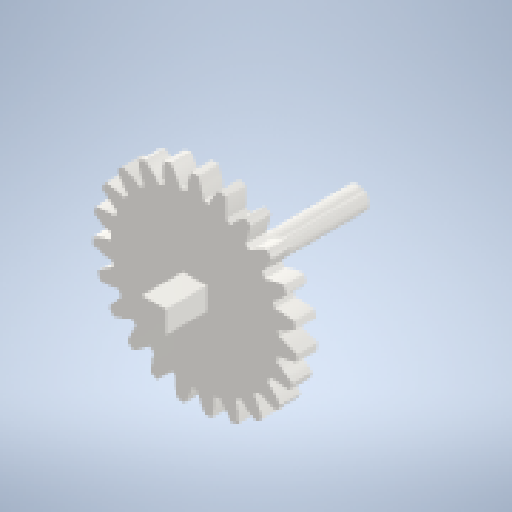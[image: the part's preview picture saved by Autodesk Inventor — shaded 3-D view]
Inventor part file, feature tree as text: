
AUTODESK INVENTOR PART (.ipt)
format: ipt  version: 2023 (Build 270158000, 158)  size: 345,600 bytes
history: native  units: mm (DEFAULTED — no unit token found)
features: sketch x4, extrude x3, plane x3, other x3, projected_geometry x1
ambient origin geometry x8: Origin, YZ Plane, XZ Plane, XY Plane, X Axis, Y Axis, Z Axis, Center Point
bodies: Solid1 (feature_tree)
feature tree (14):
  extrude  "Extrusion1"  Depth=5.0mm TaperAngle=0.0deg
  plane  "Work Plane2"
  plane  "Work Plane8"
  plane  "Work Plane9"
  other  "Spur Gear"
  extrude  "Extrusion2"  Depth=10.0mm TaperAngle=0.0deg
  extrude  "Extrusion3"  Depth=1.36591mm TaperAngle=0.0deg
  sketch  "Sketch1"  dims[d0=50.0mm d1=5.0mm d2=0.0mm]
  sketch  "Sketch2"  dims[d3=46.0mm d4=10.0mm d5=0.0mm]
  other  "Srf1"
  sketch  "Sketch3"  dims[d16=80.0mm d17=0.0mm d34=1.36591mm]
  projected_geometry  "Projected Loop1"
  sketch  "Sketch4"  dims[d39=0.0mm d41=0.0mm d43=80.0mm d46=80.0mm d47=0.0mm d48=0.0mm d49=5.5mm d50=35.0mm d51=0.0mm d52=8.0mm d54=10.0mm d55=0.0mm]
  other  "Pitch Diameter"
